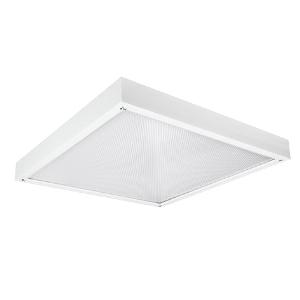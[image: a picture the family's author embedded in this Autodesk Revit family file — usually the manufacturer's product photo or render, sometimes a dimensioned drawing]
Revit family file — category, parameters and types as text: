
# Revit family: 3f_filippi_-_p_200_ip54_sp_3f_filippi_-_10860_-_p_204x10w_led_sp_ip54_596x596
name_source: partatom
category: Lighting Fixtures
units: mm (PartAtom-declared; Revit-internal decimal feet)

## family parameters
Cut with Voids When Loaded = No
Host = Face
Light Source = No
Part Type = Normal
Room Calculation Point = No
Round Connector Dimension = Use Diameter
Shared = No

## types (1)
- 3F Filippi - P 200 IP54 SP (1 x LED, 5474 lm, 45 W, 4000 K)
    Apparent Load = 45 VA
    Approval mark = ENEC
    CIE Flux Codes = 62 91 98 100 100
    Color Rendering = 80
    Color Temperature = 4000 K
    Control Gear = Electronic ballast
    Default Elevation = 1800 mm
    Description = ILLUMINOTECHNICAL
Luminous efficiency 100% (DLOR 100%, ULOR 0%).
Initial luminous flux of the luminaire 5474 lm.
Direct symmetric distribution.
Installation Interdistance Transv.D = 1.18 x hu - Long.D = 1.20 x hu.
Average luminance <3000 cd/m² for radial angles >65°.
Tabular UGR (CIE 117 - 4H-8H; S=0.25H; 70/50/20): RUG 18.7 - 18.5.
Beam angle: 91° - 92°.
Luminous efficacy 122 lm/W.
Lifetime (L93/B10): 30000 h. (tq+25°C)
Lifetime (L90/B10): 50000 h. (tq+25°C)
Lifetime (L85/B10): 80000 h. (tq+25°C)
Lifetime (L80/B10): 100000 h. (tq+25°C)
Sudden decreased luminous flux after 50000 hours: 0% (C0).
Photobiological safety in compliance with IEC/TR 62778: RG0 risk exempt, (IEC 62471).
In compliance with IEC/EN 62722-2-1 - IEC/EN 62717 standards.

SOURCE
4 linear LED modules 10W/840.
Energy efficiency class (UE 2019/2020 - UE 2019/2015): D.
CIE 13.3 Colour rendering index: CRI >80 (R9 <50%).
IES TM-30 Fidelity Index: Rf = 84 Rg = 95.
CCT nominal colour temperature 4000 K.
Colour initial tolerance (MacAdam): SDCM 2.

MECHANICAL
Housing in galvannealed steel, painted in white epoxy-polyester.
Transparent methacrylate (PMMA) flat diffuser, multilenticular exterior, anti-glare, locked to the white painted aluminium perimeter frame with sealing gasket, hinged opening.
Luminaire with limited surface temperature. - D - (EN 60598-2-24)
Dimensions: 596x596 mm, height 82 mm. Weight 5.56 kg.
IP54 protection degree.
Mechanical strength to impacts IK06 (1 joule).
Glow-wire test resistance 650°C.

ELECTRICAL
Halogen Free electronic wiring 230V-50/60Hz, power factor 0.95, THD <25%, constant output current, SELV, class I, 1 driver.
Power of the luminaire 45 W.
CE - IEC 60598-1 - EN 60598-1.
SAFE FLICKER: PstLM=<1 and SVM=<0.4 (IEC TR 61547-1 and IEC TR 63158), to ensure a more comfortable and safe light.
Luminaire compliant with EN 60598-2-22 for power supply from a centralised emergency system CPSS (Central Power Supply System), not incorporated in the luminaire - high risk areas excluded. The default power and flux are 100% in AC and 100% in DC.
Ambient temperature from 0°C to +25°C.
Temperature class T6 max 85°C.
Relative humidity UR: <85%.

INSTALLATION
Ceiling.
All accessories dedicated to this product are available on the Catalog and on our website www.3F-Filippi.com.

APPLICATIONS
Suitable product for food production plants (HACCP), IFS (Food Version 6), BRC (GSFS Food Version 7).
Environments: hospital premises, aseptic, sterilised rooms, laboratories.
Environments requiring a high level of protection, high levels of light, lamp shielding and simplified cleaning.
Environments in which there are foodstuffs or machines with moving parts, with large temperature fluctuations, and generally, in any environments that require total protection against falling fragments, SP PC version with a polycarbonate diffuser can be supplied. If necessary an L/E version i.e. with the smooth part mounted externally, or specific luminaries with laminated glass with suitable frame can also be supplied.

WARNING
Luminaire designed for disposal/recycling at end-of-life.
Replaceable (LED only) light source by a professional. Replaceable control gear by a professional.
    Height = 82 mm  [stored 0.269029 ft]
    Lamp = 1 x LED
    Lamp Light Flux = 5474 lm
    Lamp Power = 45 W
    Lamp count = 1
    Length = 596 mm
    Lifetime = 50000 h
    Luminous efficacy = 122 lm/W
    Manufacturer = 3F Filippi
    ModVariant = No
    Model = 3F Filippi - 10860 - P 204x10W LED SP IP54 596x596
    Mounting Place = Ceiling
    Mounting Type = Surface mounted
    Number of Poles = 1
    OnlyDefault = Yes
    Power Factor = 1
    Product Name = 3F Filippi - P 200 IP54 SP
    Product group = ceiling mounted luminaire
    ProductGroupID = 3
    Protection Class = Protection class I
    Protection Degree = IP 54
    RLX_Detail_Level = 1
    RLX_Emergency_Light_Flux = 0 lm
    RLX_Emergency_Type = 0
    RLX_Emergency_Type_DB = No
    RlxData = <blob elided: 39601 chars, md5=bb35f160>
    Socket = socket
    Standby Power = 0 W
    System Light Flux = 5474 lm
    System Power = 45 W
    Type Comments = Product without accessories
    Type Image = 3ffilippi_10860.jpg
    URL = http://relux.com
    VarID = ---
    Voltage = 0 V
    Weight = 0.00 kg
    Width = 596 mm

note: [stored X ft] marks values corroborated as IEEE doubles in the binary element streams (Revit-internal decimal feet)

## geometry (parser evidence)
native form markers: Blend x4, Sweep x9
no freeform markers — native parametric forms only
